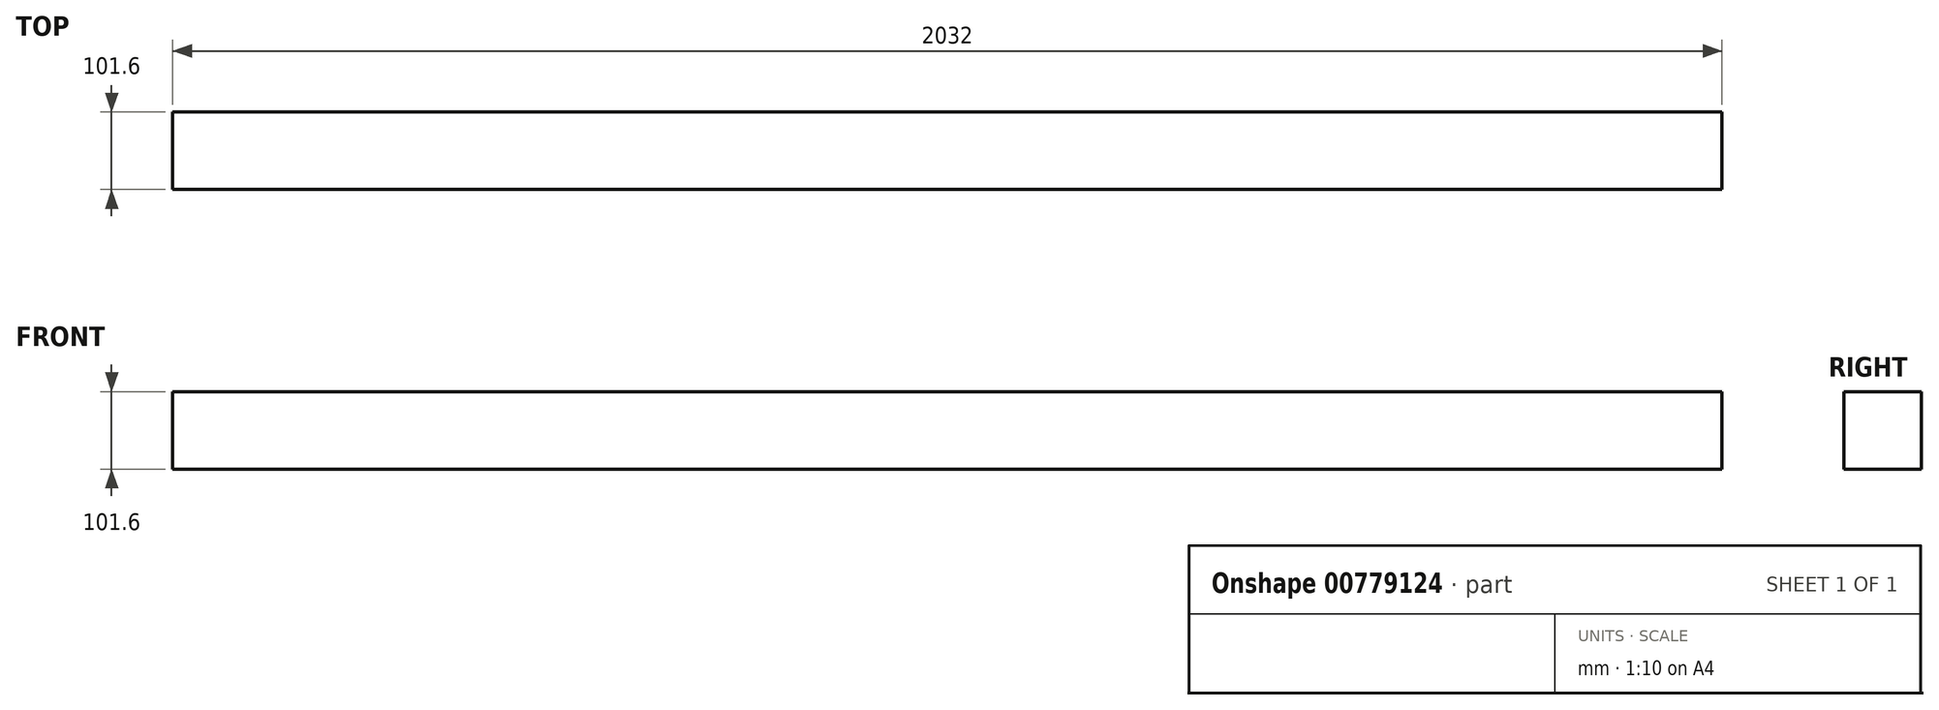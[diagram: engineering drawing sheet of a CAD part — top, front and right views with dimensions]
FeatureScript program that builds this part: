
annotation { "Feature Type Name" : "Feature", "Feature Type Description" : "" }
export const myFeature = defineFeature(function(context is Context, id is Id, definition is map)
    precondition{}
    {
        {
            var Q0;
            Q0=qCreatedBy(makeId("Right.planeOp"),FACE);
            var sketch = newSketch(context, id + "F0", { "sketchPlane" : qUnion([Q0])});
            skLineSegment(sketch, "E0.bottom", {"start": v(-50.8, 50.8) * mm, "end": v(50.8, 50.8) * mm});
            skLineSegment(sketch, "E0.top", {"start": v(-50.8, -50.8) * mm, "end": v(50.8, -50.8) * mm});
            skLineSegment(sketch, "E0.left", {"start": v(-50.8, 50.8) * mm, "end": v(-50.8, -50.8) * mm});
            skLineSegment(sketch, "E0.right", {"start": v(50.8, 50.8) * mm, "end": v(50.8, -50.8) * mm});
            skPoint(sketch, "E0.middle", {"position": v(0, 0) * mm});
            skSolve(sketch);
        }
        {
            var Q0;
            Q0 = qSketchRegion(id + "F0", true);
            extrude(context, id + "F1", {"entities" : qUnion([Q0]), "endBound" : BoundingType.SYMMETRIC, "depth" : 2032 * mm, "offsetDistance" : 25.4 * mm});
        }
    });
